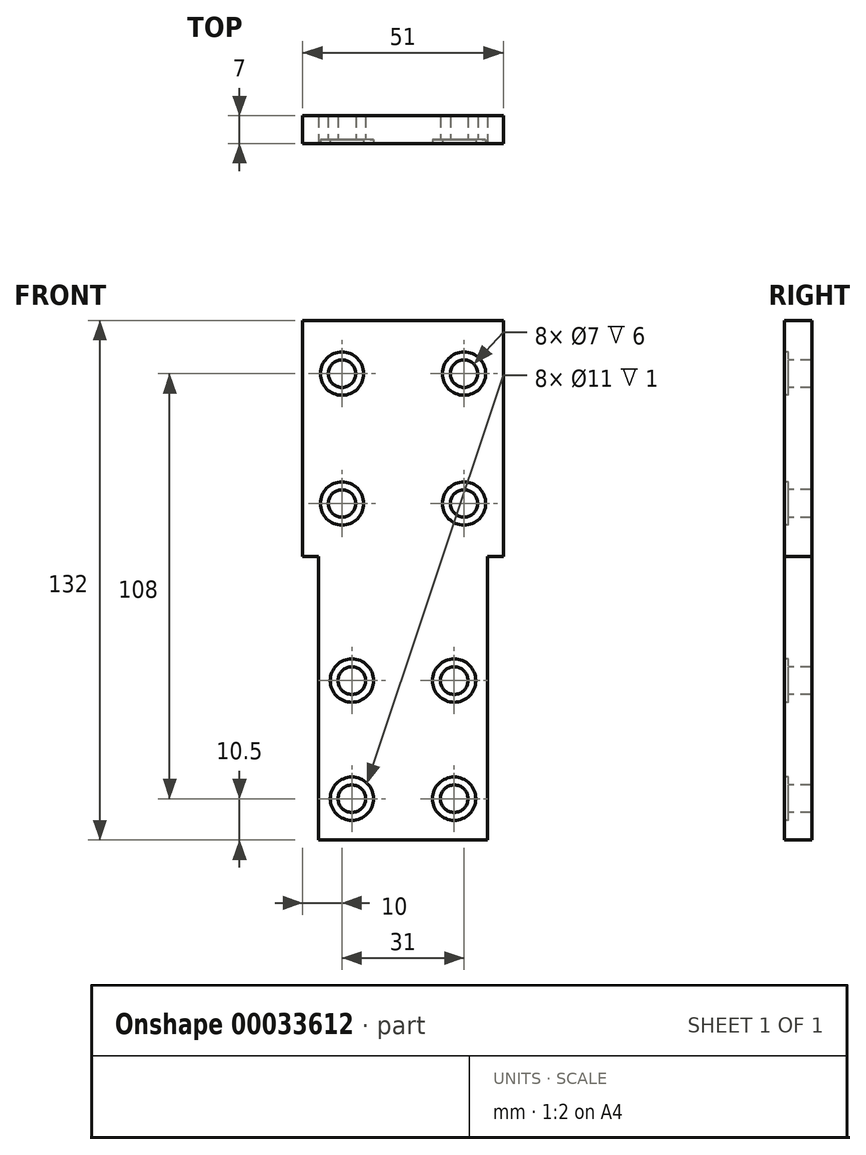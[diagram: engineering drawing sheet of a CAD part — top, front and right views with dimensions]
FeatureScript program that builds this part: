
annotation { "Feature Type Name" : "Feature", "Feature Type Description" : "" }
export const myFeature = defineFeature(function(context is Context, id is Id, definition is map)
    precondition{}
    {
        {
            var Q0;
            Q0=qCreatedBy(makeId("Front.planeOp"),FACE);
            var sketch = newSketch(context, id + "F0", { "sketchPlane" : qUnion([Q0])});
            skLineSegment(sketch, "E0.rect.bottom", {"start": v(25.5, -30) * mm, "end": v(-25.5, -30) * mm});
            skLineSegment(sketch, "E0.rect.top", {"start": v(25.5, 30) * mm, "end": v(-25.5, 30) * mm});
            skLineSegment(sketch, "E0.rect.left", {"start": v(25.5, -30) * mm, "end": v(25.5, 30) * mm});
            skLineSegment(sketch, "E0.rect.right", {"start": v(-25.5, -30) * mm, "end": v(-25.5, 30) * mm});
            skPoint(sketch, "E0.rect.middle", {"position": v(0, 0) * mm});
            skSolve(sketch);
        }
        {
            var Q0;
            Q0 = qSketchRegion(id + "F0", true);
            extrude(context, id + "F1", {"entities" : qUnion([Q0]), "depth" : 7 * mm});
        }
        {
            var Q0;
            Q0=makeQuery(id+"F1.opExtrude","CAP_FACE",FACE,{"disambiguationData":[OSD([sQuery(id+"F0.wireOp",EDGE,"E0.rect.bottom"),sQuery(id+"F0.wireOp",EDGE,"E0.rect.top"),sQuery(id+"F0.wireOp",EDGE,"E0.rect.left"),sQuery(id+"F0.wireOp",EDGE,"E0.rect.right")])],"isStart":false});
            var sketch = newSketch(context, id + "F2", { "sketchPlane" : qUnion([Q0])});
            skLineSegment(sketch, "E1", {"start": v(-15.5, 30) * mm, "end": v(-15.5, -30) * mm, "construction": true});
            skLineSegment(sketch, "E2", {"start": v(15.5, 30) * mm, "end": v(15.5, -30) * mm, "construction": true});
            skCircle(sketch, "E3", {"center": v(-15.5, 16.5) * mm, "radius": 3.5 * mm});
            skCircle(sketch, "E4", {"center": v(-15.5, -16.5) * mm, "radius": 3.5 * mm});
            skCircle(sketch, "E5", {"center": v(15.5, 16.5) * mm, "radius": 3.5 * mm});
            skCircle(sketch, "E6", {"center": v(15.5, -16.5) * mm, "radius": 3.5 * mm});
            skSolve(sketch);
        }
        {
            var Q0;
            Q0 = qSketchRegion(id + "F2", true);
            extrude(context, id + "F3", {"entities" : qUnion([Q0]), "operationType" : NewBodyOperationType.REMOVE, "oppositeDirection" : true, "depth" : 25 * mm});
        }
        {
            var Q0;
            Q0=makeQuery(id+"F1.opExtrude","CAP_FACE",FACE,{"disambiguationData":[OSD([sQuery(id+"F0.wireOp",EDGE,"E0.rect.bottom"),sQuery(id+"F0.wireOp",EDGE,"E0.rect.top"),sQuery(id+"F0.wireOp",EDGE,"E0.rect.left"),sQuery(id+"F0.wireOp",EDGE,"E0.rect.right")])],"isStart":false});
            var sketch = newSketch(context, id + "F4", { "sketchPlane" : qUnion([Q0])});
            skCircle(sketch, "E7", {"center": v(-15.5, 16.5) * mm, "radius": 5.5 * mm});
            skCircle(sketch, "E8", {"center": v(-15.5, -16.5) * mm, "radius": 5.5 * mm});
            skCircle(sketch, "E9", {"center": v(15.5, -16.5) * mm, "radius": 5.5 * mm});
            skCircle(sketch, "E10", {"center": v(15.5, 16.5) * mm, "radius": 5.5 * mm});
            skSolve(sketch);
        }
        {
            var Q0;
            Q0 = qSketchRegion(id + "F4", true);
            extrude(context, id + "F5", {"entities" : qUnion([Q0]), "operationType" : NewBodyOperationType.REMOVE, "oppositeDirection" : true, "depth" : 1 * mm});
        }
        {
            var Q0;
            Q0=makeQuery(id+"F1.opExtrude","CAP_FACE",FACE,{"disambiguationData":[OSD([sQuery(id+"F0.wireOp",EDGE,"E0.rect.bottom"),sQuery(id+"F0.wireOp",EDGE,"E0.rect.top"),sQuery(id+"F0.wireOp",EDGE,"E0.rect.left"),sQuery(id+"F0.wireOp",EDGE,"E0.rect.right")])],"isStart":false});
            var sketch = newSketch(context, id + "F6", { "sketchPlane" : qUnion([Q0])});
            skLineSegment(sketch, "E11.bottom", {"start": v(-21.5, -30) * mm, "end": v(21.5, -30) * mm});
            skLineSegment(sketch, "E11.top", {"start": v(-21.5, -110) * mm, "end": v(21.5, -110) * mm});
            skLineSegment(sketch, "E11.left", {"start": v(-21.5, -30) * mm, "end": v(-21.5, -110) * mm});
            skLineSegment(sketch, "E11.right", {"start": v(21.5, -30) * mm, "end": v(21.5, -110) * mm});
            skSolve(sketch);
        }
        {
            var Q0;
            Q0 = qSketchRegion(id + "F6", true);
            extrude(context, id + "F7", {"entities" : qUnion([Q0]), "oppositeDirection" : true, "depth" : 7 * mm});
        }
        {
            var Q0;
            Q0=makeQuery(id+"F1.opExtrude","SWEPT_BODY",BODY,{"disambiguationData":[OSD([sQuery(id+"F0.wireOp",EDGE,"E0.rect.bottom"),sQuery(id+"F0.wireOp",EDGE,"E0.rect.top"),sQuery(id+"F0.wireOp",EDGE,"E0.rect.left"),sQuery(id+"F0.wireOp",EDGE,"E0.rect.right")])]});
            var Q1;
            Q1=makeQuery(id+"F7.opExtrude","SWEPT_BODY",BODY,{"disambiguationData":[OSD([sQuery(id+"F6.wireOp",EDGE,"E11.bottom"),sQuery(id+"F6.wireOp",EDGE,"E11.top"),sQuery(id+"F6.wireOp",EDGE,"E11.left"),sQuery(id+"F6.wireOp",EDGE,"E11.right")])]});
            booleanBodies(context, id + "F8", {"operationType" : BooleanOperationType.UNION, "tools" : qUnion([Q0, Q1])});
        }
        {
            var Q0;
            Q0=makeQuery(id+"F8.opBoolean","MERGE",FACE,{"derivedFrom":[makeQuery(id+"F1.opExtrude","CAP_FACE",FACE,{"disambiguationData":[OSD([sQuery(id+"F0.wireOp",EDGE,"E0.rect.bottom"),sQuery(id+"F0.wireOp",EDGE,"E0.rect.top"),sQuery(id+"F0.wireOp",EDGE,"E0.rect.left"),sQuery(id+"F0.wireOp",EDGE,"E0.rect.right")])],"isStart":false}),makeQuery(id+"F7.opExtrude","CAP_FACE",FACE,{"disambiguationData":[OSD([sQuery(id+"F6.wireOp",EDGE,"E11.bottom"),sQuery(id+"F6.wireOp",EDGE,"E11.top"),sQuery(id+"F6.wireOp",EDGE,"E11.left"),sQuery(id+"F6.wireOp",EDGE,"E11.right")])],"isStart":true})]});
            var sketch = newSketch(context, id + "F9", { "sketchPlane" : qUnion([Q0])});
            skCircle(sketch, "E12", {"center": v(-13, -61.5) * mm, "radius": 3.5 * mm});
            skCircle(sketch, "E13", {"center": v(13, -61.5) * mm, "radius": 3.5 * mm});
            skCircle(sketch, "E14", {"center": v(-13, -91.5) * mm, "radius": 3.5 * mm});
            skCircle(sketch, "E15", {"center": v(13, -91.5) * mm, "radius": 3.5 * mm});
            skLineSegment(sketch, "E16", {"start": v(-21.5, -30) * mm, "end": v(21.5, -30) * mm, "construction": true});
            skLineSegment(sketch, "E17", {"start": v(21.5, -30) * mm, "end": v(21.5, -110) * mm, "construction": true});
            skLineSegment(sketch, "E18", {"start": v(21.5, -110) * mm, "end": v(-21.5, -110) * mm, "construction": true});
            skLineSegment(sketch, "E19", {"start": v(-21.5, -110) * mm, "end": v(-21.5, -30) * mm, "construction": true});
            skSolve(sketch);
        }
        {
            var Q0;
            Q0 = qSketchRegion(id + "F9", true);
            extrude(context, id + "F10", {"entities" : qUnion([Q0]), "operationType" : NewBodyOperationType.REMOVE, "oppositeDirection" : true, "depth" : 25 * mm});
        }
        {
            var Q0;
            Q0=makeQuery(id+"F8.opBoolean","MERGE",FACE,{"derivedFrom":[makeQuery(id+"F1.opExtrude","CAP_FACE",FACE,{"disambiguationData":[OSD([sQuery(id+"F0.wireOp",EDGE,"E0.rect.bottom"),sQuery(id+"F0.wireOp",EDGE,"E0.rect.top"),sQuery(id+"F0.wireOp",EDGE,"E0.rect.left"),sQuery(id+"F0.wireOp",EDGE,"E0.rect.right")])],"isStart":false}),makeQuery(id+"F7.opExtrude","CAP_FACE",FACE,{"disambiguationData":[OSD([sQuery(id+"F6.wireOp",EDGE,"E11.bottom"),sQuery(id+"F6.wireOp",EDGE,"E11.top"),sQuery(id+"F6.wireOp",EDGE,"E11.left"),sQuery(id+"F6.wireOp",EDGE,"E11.right")])],"isStart":true})]});
            var sketch = newSketch(context, id + "F11", { "sketchPlane" : qUnion([Q0])});
            skCircle(sketch, "E20", {"center": v(-13, -61.5) * mm, "radius": 5.5 * mm});
            skCircle(sketch, "E21", {"center": v(13, -61.5) * mm, "radius": 5.5 * mm});
            skCircle(sketch, "E22", {"center": v(-13, -91.5) * mm, "radius": 5.5 * mm});
            skCircle(sketch, "E23", {"center": v(13, -91.5) * mm, "radius": 5.5 * mm});
            skSolve(sketch);
        }
        {
            var Q0;
            Q0 = qSketchRegion(id + "F11", true);
            extrude(context, id + "F12", {"entities" : qUnion([Q0]), "operationType" : NewBodyOperationType.REMOVE, "oppositeDirection" : true, "depth" : 1 * mm});
        }
        {
            var Q0;
            Q0=makeQuery(id+"F8.opBoolean","MERGE",FACE,{"derivedFrom":[makeQuery(id+"F1.opExtrude","CAP_FACE",FACE,{"disambiguationData":[OSD([sQuery(id+"F0.wireOp",EDGE,"E0.rect.bottom"),sQuery(id+"F0.wireOp",EDGE,"E0.rect.top"),sQuery(id+"F0.wireOp",EDGE,"E0.rect.left"),sQuery(id+"F0.wireOp",EDGE,"E0.rect.right")])],"isStart":false}),makeQuery(id+"F7.opExtrude","CAP_FACE",FACE,{"disambiguationData":[OSD([sQuery(id+"F6.wireOp",EDGE,"E11.bottom"),sQuery(id+"F6.wireOp",EDGE,"E11.top"),sQuery(id+"F6.wireOp",EDGE,"E11.left"),sQuery(id+"F6.wireOp",EDGE,"E11.right")])],"isStart":true})]});
            var sketch = newSketch(context, id + "F13", { "sketchPlane" : qUnion([Q0])});
            skLineSegment(sketch, "E24.bottom", {"start": v(-21.5, -102) * mm, "end": v(21.5, -102) * mm});
            skLineSegment(sketch, "E24.top", {"start": v(-21.5, -110) * mm, "end": v(21.5, -110) * mm});
            skLineSegment(sketch, "E24.left", {"start": v(-21.5, -102) * mm, "end": v(-21.5, -110) * mm});
            skLineSegment(sketch, "E24.right", {"start": v(21.5, -102) * mm, "end": v(21.5, -110) * mm});
            skSolve(sketch);
        }
        {
            var Q0;
            Q0 = qSketchRegion(id + "F13", true);
            extrude(context, id + "F14", {"entities" : qUnion([Q0]), "operationType" : NewBodyOperationType.REMOVE, "oppositeDirection" : true, "depth" : 25 * mm});
        }
    });
